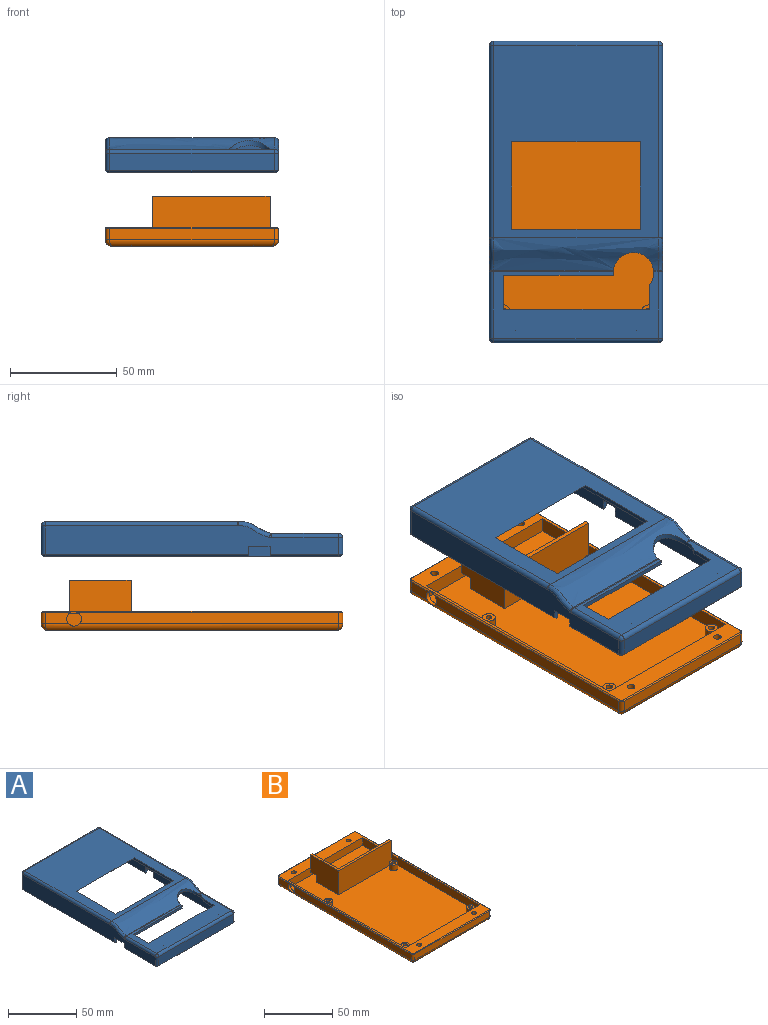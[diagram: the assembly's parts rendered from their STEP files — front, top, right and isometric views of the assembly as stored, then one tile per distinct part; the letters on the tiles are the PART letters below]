
ASSEMBLY  parts=2 mates=1
PART A: 72 faces, bbox 81x141x16.5 mm
  f0: plane 77x23.74mm, normal (0,0,-1), area 690.5mm2, adj f5,f9,f14,f48,f63,f64,f65,f66
  f1: plane 89.96x77mm, normal (0,0,1), area 4466.7mm2, adj f27,f32,f35,f38,f68,f69,f70,f71
  f2: extruded ~77x15.22mm, area 1132.5mm2, adj f6,f7,f33,f34,f38,f67
  f3: plane 77x31.26mm, normal (0,0,1), area 1278.7mm2, adj f6,f7,f19,f24,f25,f63,f64,f65
  f4: plane 82.04x77mm, normal (0,0,-1), area 3737.4mm2, adj f5,f9,f14,f47,f68,f69,f70,f71
  f5: extruded ~77x15.22mm, area 1134.9mm2, adj f0,f4,f9,f14,f67
  f6: cylinder r=2mm len=2.21mm, axis (-1,0,0), area 1.1mm2, adj f2,f3,f29,f67
  f7: cylinder r=2mm len=55.91mm, axis (-1,0,0), area 27.3mm2, adj f2,f3,f30,f67
  f8: plane 82x79mm, normal (0,0,-1), area 790.5mm2, adj f9,f10,f14,f39,f40,f42,f44,f48
  f9: plane 121x14.52mm, normal (-1,0,0), area 1547.7mm2, adj f0,f4,f5,f8,f11,f47,f48,f60
  f10: plane 81x1mm, normal (0.71,0,-0.71), area 114.6mm2, adj f8,f17,f39,f62
  f11: plane 96x79mm, normal (0,0,-1), area 820.5mm2, adj f9,f13,f14,f41,f43,f45,f46,f47
  f12: plane 137x13.52mm, normal (-1,0,0), area 1598.7mm2, adj f13,f20,f25,f26,f30,f34,f35,f37
  f13: plane 95x1mm, normal (-0.71,0,-0.71), area 134.4mm2, adj f11,f12,f46,f59
  f14: plane 121x14.52mm, normal (1,0,0), area 1537.7mm2, adj f0,f4,f5,f8,f11,f47,f48,f57
  f15: plane 77x8mm, normal (0,-1,0), area 616mm2, adj f18,f19,f20,f40
  f16: plane 77x13.5mm, normal (0,1,0), area 1039.5mm2, adj f23,f26,f27,f45
  f17: plane 137x13.52mm, normal (1,0,0), area 1606.7mm2, adj f10,f18,f23,f24,f29,f32,f33,f36
  f18: cylinder r=2mm len=8mm, axis (0,0,1), area 25.1mm2, adj f15,f17,f21,f39
  f19: cylinder r=2mm len=77mm, axis (-1,0,0), area 241.9mm2, adj f3,f15,f21,f22
  f20: cylinder r=2mm len=8mm, axis (0,0,-1), area 25.1mm2, adj f12,f15,f22,f42
  f21: sphere r=2mm, area 6.3mm2, adj f18,f19,f24
  f22: sphere r=2mm, area 6.3mm2, adj f19,f20,f25
  f23: cylinder r=2mm len=13.5mm, axis (0,0,-1), area 42.4mm2, adj f16,f17,f28,f43
  f24: cylinder r=2mm len=31.26mm, axis (0,1,0), area 98.2mm2, adj f3,f17,f21,f29
  f25: cylinder r=2mm len=31.26mm, axis (0,-1,0), area 98.2mm2, adj f3,f12,f22,f30
  f26: cylinder r=2mm len=13.5mm, axis (0,0,1), area 42.4mm2, adj f12,f16,f31,f46
  f27: cylinder r=2mm len=77mm, axis (-1,0,0), area 241.9mm2, adj f1,f16,f28,f31
  f28: sphere r=2mm, area 6.3mm2, adj f23,f27,f32
  f29: torus R=4mm, axis (1,0,0), area 2.1mm2, adj f6,f17,f24,f33
  f30: torus R=4mm, axis (1,0,0), area 2.1mm2, adj f7,f12,f25,f34
  f31: sphere r=2mm, area 6.3mm2, adj f26,f27,f35
  f32: cylinder r=2mm len=89.96mm, axis (0,1,0), area 282.6mm2, adj f1,f17,f28,f36
  f33: bspline ~19.24x7.56mm, area 51mm2, adj f2,f17,f29,f36
  f34: bspline ~19.24x7.56mm, area 51mm2, adj f2,f12,f30,f37
  f35: cylinder r=2mm len=89.96mm, axis (0,-1,0), area 282.6mm2, adj f1,f12,f31,f37
  f36: torus R=4mm, axis (1,0,0), area 0.4mm2, adj f17,f32,f33,f38
  f37: torus R=4mm, axis (1,0,0), area 0.4mm2, adj f12,f34,f35,f38
  f38: cylinder r=2mm len=77mm, axis (-1,0,0), area 6.6mm2, adj f1,f2,f36,f37
  f39: cone r=1mm half-angle=45deg, axis (0,0,1), area 3.3mm2, adj f8,f10,f18,f40
  f40: plane 77x1mm, normal (0,-0.71,-0.71), area 108.9mm2, adj f8,f15,f39,f42
  f41: plane 48x1mm, normal (0.71,0,-0.71), area 67.9mm2, adj f11,f17,f43,f60
  f42: cone r=1mm half-angle=45deg, axis (0,0,1), area 3.3mm2, adj f8,f20,f40,f44
  f43: cone r=1mm half-angle=45deg, axis (0,0,1), area 3.3mm2, adj f11,f23,f41,f45
  f44: plane 32x1mm, normal (-0.71,0,-0.71), area 45.3mm2, adj f8,f12,f42,f57
  f45: plane 77x1mm, normal (0,0.71,-0.71), area 108.9mm2, adj f11,f16,f43,f46
  f46: cone r=1mm half-angle=45deg, axis (0,0,1), area 3.3mm2, adj f11,f13,f26,f45
  f47: plane 77x14.5mm, normal (0,-1,0), area 1116.5mm2, adj f4,f9,f11,f14
  f48: plane 77x9mm, normal (0,1,0), area 693mm2, adj f0,f8,f9,f14
  f49: cylinder r=1.65mm len=10mm, axis (0,0,-1), area 103.7mm2, adj f8,f50
  f50: cone r=0mm half-angle=59deg, axis (0,0,-1), area 10mm2, adj f49
  f51: cylinder r=1.65mm len=10mm, axis (0,0,-1), area 103.7mm2, adj f8,f52
  f52: cone r=0mm half-angle=59deg, axis (0,0,-1), area 10mm2, adj f51
  f53: cylinder r=1.65mm len=10mm, axis (0,0,-1), area 103.7mm2, adj f11,f54
  f54: cone r=0mm half-angle=59deg, axis (0,0,-1), area 10mm2, adj f53
  f55: cylinder r=1.65mm len=10mm, axis (0,0,-1), area 103.7mm2, adj f11,f56
  f56: cone r=0mm half-angle=59deg, axis (0,0,-1), area 10mm2, adj f55
  f57: plane 5x2mm, normal (0,1,0), area 9.5mm2, adj f8,f12,f14,f44,f58
  f58: plane 10x2mm, normal (0,0,-1), area 20mm2, adj f12,f14,f57,f59
  f59: plane 5x2mm, normal (0,-1,0), area 9.5mm2, adj f11,f12,f13,f14,f58
  f60: plane 5x2mm, normal (0,-1,0), area 9.5mm2, adj f9,f11,f17,f41,f61
  f61: plane 8x2mm, normal (0,0,-1), area 16mm2, adj f9,f17,f60,f62
  f62: plane 5x2mm, normal (0,1,0), area 9.5mm2, adj f8,f9,f10,f17,f61
  f63: plane 11.23x2mm, normal (-1,0,0), area 22.5mm2, adj f0,f3,f66,f67
  f64: plane 51.22x2mm, normal (0,-1,0), area 102.4mm2, adj f0,f3,f65,f67
  f65: plane 16x2mm, normal (1,0,0), area 32mm2, adj f0,f3,f64,f66
  f66: plane 68.05x2mm, normal (0,1,0), area 136.1mm2, adj f0,f3,f63,f65
  f67: cylinder r=9.5mm len=19mm, axis (0,0,-1), area 82.5mm2, adj f0,f2,f3,f5,f6,f7,f63,f64
  f68: plane 43x2mm, normal (1,0,0), area 84mm2, adj f1,f4,f69,f71
  f69: plane 60x2mm, normal (0,1,0), area 120mm2, adj f1,f4,f68,f70
  f70: plane 43x2mm, normal (-1,0,0), area 84mm2, adj f1,f4,f69,f71
  f71: plane 60x2mm, normal (0,-0.71,-0.71), area 169.7mm2, adj f1,f4,f68,f70
PART B: 70 faces, bbox 81x141x23.5 mm
  f0: plane 11.82x5.5mm, normal (-1,0,0), area 56.9mm2, adj f2,f8,f43,f48
  f1: plane 15.5x2mm, normal (0,1,0), area 31mm2, adj f38,f39,f42,f45
  f2: plane 137x0.5mm, normal (-0.71,0,0.71), area 95.9mm2, adj f0,f9,f15,f16,f18,f43
  f3: plane 121x77mm, normal (0,0,1), area 9051.9mm2, adj f4,f5,f23,f24,f37,f39,f40,f41
  f4: plane 121x7mm, normal (1,0,0), area 810.1mm2, adj f3,f15,f23,f24,f43
  f5: plane 121x7mm, normal (-1,0,0), area 847mm2, adj f3,f15,f23,f24
  f6: cylinder r=2mm len=5.5mm, axis (0,0,1), area 17.3mm2, adj f7,f13,f19,f49
  f7: plane 77x5.5mm, normal (0,1,0), area 423.5mm2, adj f6,f8,f17,f47
  f8: cylinder r=2mm len=5.5mm, axis (0,0,1), area 17.3mm2, adj f0,f7,f16,f46
  f9: plane 122.17x5.5mm, normal (-1,0,0), area 663.8mm2, adj f2,f10,f43,f48
  f10: cylinder r=2mm len=5.5mm, axis (0,0,1), area 17.3mm2, adj f9,f11,f18,f50
  f11: plane 77x5.5mm, normal (0,-1,0), area 423.5mm2, adj f10,f12,f20,f52
  f12: cylinder r=2mm len=5.5mm, axis (0,0,1), area 17.3mm2, adj f11,f13,f22,f53
  f13: plane 137x5.5mm, normal (1,0,0), area 753.5mm2, adj f6,f12,f21,f51
  f14: plane 135x75mm, normal (0,0,-1), area 9984.6mm2, adj f27,f30,f33,f36,f47,f48,f51,f52
  f15: plane 140x80mm, normal (0,0,1), area 1842.6mm2, adj f2,f4,f5,f16,f17,f18,f19,f20
  f16: cone r=1.5mm half-angle=45deg, axis (0,0,-1), area 1.9mm2, adj f2,f8,f15,f17
  f17: plane 77x0.5mm, normal (0,0.71,0.71), area 54.4mm2, adj f7,f15,f16,f19
  f18: cone r=1.5mm half-angle=45deg, axis (0,0,-1), area 1.9mm2, adj f2,f10,f15,f20
  f19: cone r=1.5mm half-angle=45deg, axis (0,0,-1), area 1.9mm2, adj f6,f15,f17,f21
  f20: plane 77x0.5mm, normal (0,-0.71,0.71), area 54.4mm2, adj f11,f15,f18,f22
  f21: plane 137x0.5mm, normal (0.71,0,0.71), area 96.9mm2, adj f13,f15,f19,f22
  f22: cone r=1.5mm half-angle=45deg, axis (0,0,-1), area 1.9mm2, adj f12,f15,f20,f21
  f23: plane 77x7mm, normal (0,-1,0), area 539mm2, adj f3,f4,f5,f15
  f24: plane 77x7mm, normal (0,1,0), area 539mm2, adj f3,f4,f5,f15
  f25: cylinder r=1.75mm len=6mm, axis (0,0,-1), area 66mm2, adj f15,f26
  f26: plane 7x7mm, normal (0,0,-1), area 28.9mm2, adj f25,f27
  f27: cylinder r=3.5mm len=7mm, axis (0,0,-1), area 65.5mm2, adj f14,f26,f47
  f28: cylinder r=1.75mm len=6mm, axis (0,0,-1), area 66mm2, adj f15,f29
  f29: plane 7x7mm, normal (0,0,-1), area 28.9mm2, adj f28,f30
  f30: cylinder r=3.5mm len=7mm, axis (0,0,-1), area 65.5mm2, adj f14,f29,f47
  f31: cylinder r=1.75mm len=6mm, axis (0,0,-1), area 66mm2, adj f15,f32
  f32: plane 7x7mm, normal (0,0,-1), area 28.9mm2, adj f31,f33
  f33: cylinder r=3.5mm len=7mm, axis (0,0,-1), area 65.5mm2, adj f14,f32,f52
  f34: cylinder r=1.75mm len=6mm, axis (0,0,-1), area 66mm2, adj f15,f35
  f35: plane 7x7mm, normal (0,0,-1), area 28.9mm2, adj f34,f36
  f36: cylinder r=3.5mm len=7mm, axis (0,0,-1), area 65.5mm2, adj f14,f35,f52
  f37: plane 55x21.5mm, normal (0,-1,0), area 1182.5mm2, adj f3,f38,f39,f40
  f38: plane 55x29mm, normal (0,0,1), area 164mm2, adj f1,f37,f39,f40,f41,f42
  f39: plane 29x21.5mm, normal (-1,0,0), area 587.5mm2, adj f1,f3,f37,f38,f44,f45
  f40: plane 21.5x2mm, normal (1,0,0), area 43mm2, adj f3,f37,f38,f41
  f41: plane 53x21.5mm, normal (0,1,0), area 1139.5mm2, adj f3,f38,f40,f42
  f42: plane 27x21.5mm, normal (1,0,0), area 544.5mm2, adj f1,f3,f38,f41,f44,f45
  f43: cylinder r=3.43mm len=6.85mm, axis (-1,0,0), area 41.8mm2, adj f0,f2,f4,f9,f48
  f44: plane 6x2mm, normal (0,1,0), area 12mm2, adj f3,f39,f42,f45
  f45: plane 6x2mm, normal (0,0,-1), area 12mm2, adj f1,f39,f42,f44
  f46: bspline ~3.16x3mm, area 9.7mm2, adj f8,f47,f48
  f47: cylinder r=3mm len=77mm, axis (1,0,0), area 352.6mm2, adj f7,f14,f27,f30,f46,f49
  f48: cylinder r=3mm len=137mm, axis (0,1,0), area 638.8mm2, adj f0,f9,f14,f43,f46,f50
  f49: bspline ~3.16x3mm, area 9.7mm2, adj f6,f47,f51
  f50: bspline ~3.16x3mm, area 9.7mm2, adj f10,f48,f52
  f51: cylinder r=3mm len=137mm, axis (0,-1,0), area 642.2mm2, adj f13,f14,f49,f53
  f52: cylinder r=3mm len=77mm, axis (-1,0,0), area 352.6mm2, adj f11,f14,f33,f36,f50,f53
  f53: bspline ~3.16x3mm, area 9.7mm2, adj f12,f51,f52
  f54: cylinder r=3mm len=6mm, axis (0,0,-1), area 94.2mm2, adj f3,f55
  f55: plane 6x6mm, normal (0,0,1), area 21.2mm2, adj f54,f68
  f56: cylinder r=3mm len=6mm, axis (0,0,-1), area 94.2mm2, adj f3,f57
  f57: plane 6x6mm, normal (0,0,1), area 21.2mm2, adj f56,f66
  f58: cylinder r=3mm len=6mm, axis (0,0,-1), area 94.2mm2, adj f3,f59
  f59: plane 6x6mm, normal (0,0,1), area 21.2mm2, adj f58,f64
  f60: cylinder r=3mm len=6mm, axis (0,0,-1), area 94.2mm2, adj f3,f61
  f61: plane 6x6mm, normal (0,0,1), area 22.3mm2, adj f60,f62
  f62: cylinder r=1.38mm len=5mm, axis (0,0,-1), area 43.2mm2, adj f61,f63
  f63: plane 2.75x2.75mm, normal (0,0,1), area 5.9mm2, adj f62
  f64: cylinder r=1.5mm len=5mm, axis (0,0,-1), area 47.1mm2, adj f59,f65
  f65: plane 3x3mm, normal (0,0,1), area 7.1mm2, adj f64
  f66: cylinder r=1.5mm len=5mm, axis (0,0,-1), area 47.1mm2, adj f57,f67
  f67: plane 3x3mm, normal (0,0,1), area 7.1mm2, adj f66
  f68: cylinder r=1.5mm len=5mm, axis (0,0,-1), area 47.1mm2, adj f55,f69
  f69: plane 3x3mm, normal (0,0,1), area 7.1mm2, adj f68
PLACE A t=(-28.54,52.81,13.06)mm
PLACE B t=(-28.54,52.81,-12.28)mm
MATE slider B.f15 <-> A.f8  axis (0,0,-1) through (-28.54,52.81,-12.28)mm
